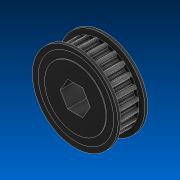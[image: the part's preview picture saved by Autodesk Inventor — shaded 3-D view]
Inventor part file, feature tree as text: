
AUTODESK INVENTOR PART (.ipt)
format: ipt  version: 2022.2 (Build 262287000, 287)  size: 657,920 bytes
history: native  units: in
note: dims shown in document units (in); Inventor stores cm internally (conversion verified against a paired STEP export)
features: mirror x1
ambient origin geometry x8: Origin, YZ Plane, XZ Plane, XY Plane, X Axis, Y Axis, Z Axis, Center Point
bodies: Solid1 (feature_tree)
feature tree (1):
  mirror  "Mirror1"
